# Revit family: Deca_Torneira Lavatório Tube_1199.C.TUB.PSO_Piso
name_source: partatom
category: Plumbing Fixtures
revit_build: Autodesk Revit Architecture 2012 (Build: 20120126_0600(x64)
units: mm (PartAtom-declared; Revit-internal decimal feet)

## types (1)
- 1199.C.TUB.PSO_Cromado CR10
    Aprovado por = Contino/quattroD
    Assembly Code = D2020
    Atendimento ao Cliente = 0800-0117073
    CWFU = 0
    Chuveiro = Deca CR10 Cromado Metal
    Consumo = Varia com a pressão
    Criado por = Contino/quattroD
    Código = 1199.C.TUB.PSO
    Default Elevation = 0 mm  [stored 0 ft]
    Description = Torneira Lavatório de Piso
    Diâmetro Água Fria = 15 mm  [stored 0.0492126 ft]
    Flow Pressure = 0.00 psi
    HWFU = 0
    Informações Complementares = Mecanismo: 1/4 de volta
    Linha = Tube
    Louça/Metais = Metal
    Manufacturer = Deca
    Material = Deca_Latão Cromado e Plástico de Engenharia
    Model = 1199.C.TUB.PSO
    Norma = ABNT NBR 15748: 2009
    Peso Liquido (Kg) = 3.72
    Pressão = 2 A 40 mca
    Produto = Torneira Lavatório de Piso Tube
    Raio Água Fria = 8 mm  [stored 0.0262467 ft]
    Segmento = Luxo
    URL = www.deca.com.br/produtos
    Variações de COR = Cromado (1199.C.TUB.PSO)
    WFU = 0

note: [stored X ft] marks values corroborated as IEEE doubles in the binary element streams (Revit-internal decimal feet)

## geometry (parser evidence)
native form markers: Blend x4, Sweep x1
no freeform markers — native parametric forms only
